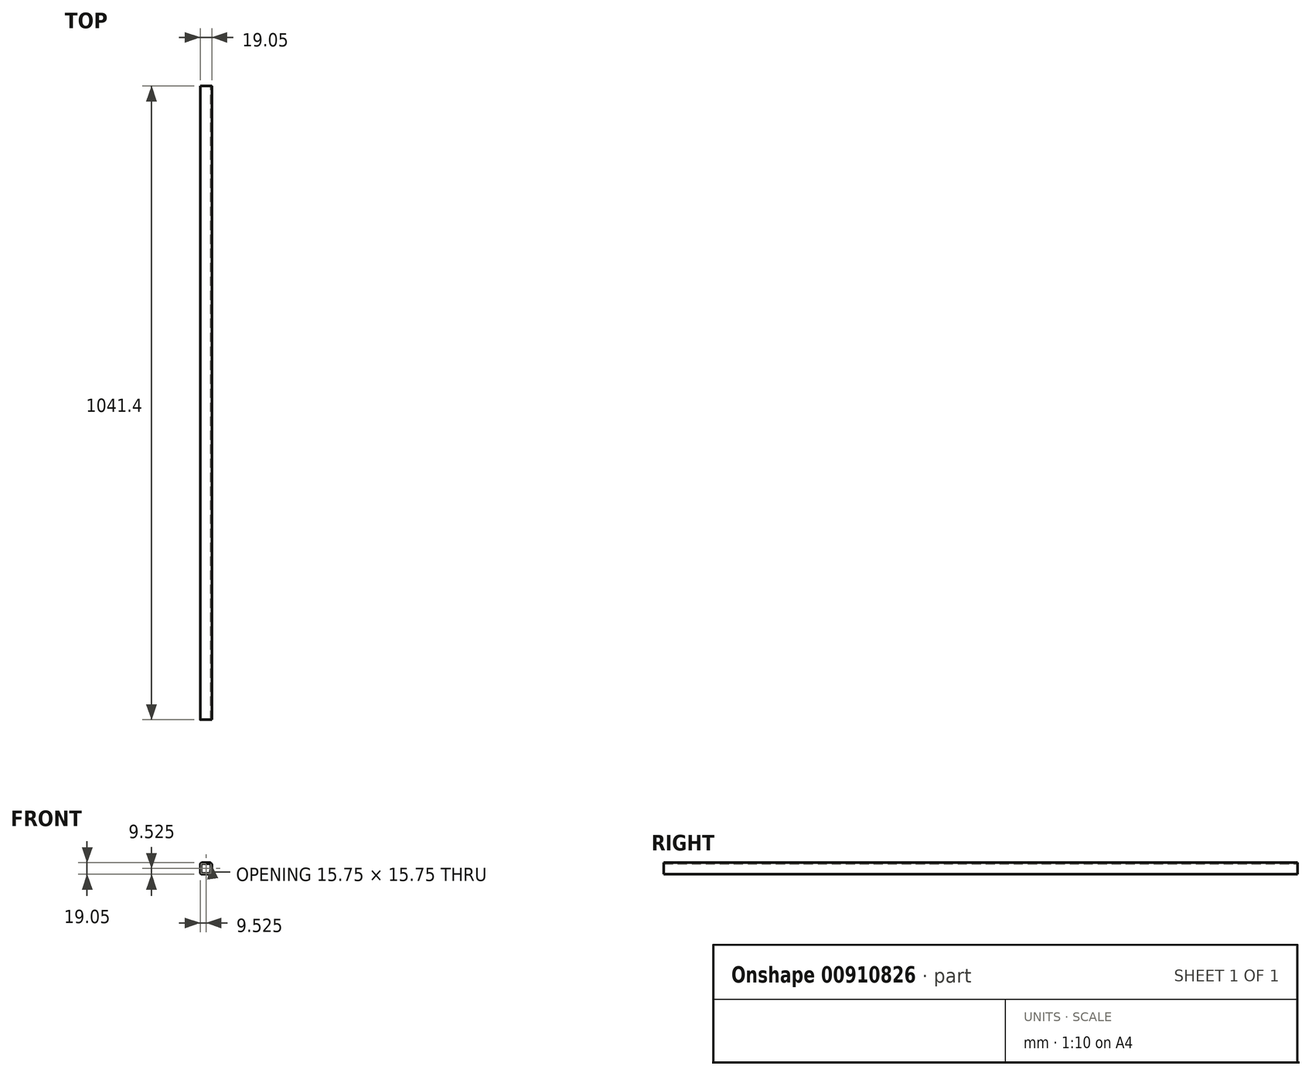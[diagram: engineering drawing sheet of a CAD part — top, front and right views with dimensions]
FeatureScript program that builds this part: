
annotation { "Feature Type Name" : "Feature", "Feature Type Description" : "" }
export const myFeature = defineFeature(function(context is Context, id is Id, definition is map)
    precondition{}
    {
        {
            var Q0;
            Q0=qCreatedBy(makeId("Front.planeOp"),FACE);
            var sketch = newSketch(context, id + "F0", { "sketchPlane" : qUnion([Q0])});
            skLineSegment(sketch, "E0.bottom", {"start": v(3.18, 0) * mm, "end": v(15.87, 0) * mm});
            skLineSegment(sketch, "E0.top", {"start": v(3.17, 19.05) * mm, "end": v(15.88, 19.05) * mm});
            skLineSegment(sketch, "E0.left", {"start": v(0, 3.17) * mm, "end": v(0, 15.88) * mm});
            skLineSegment(sketch, "E0.right", {"start": v(19.05, 3.18) * mm, "end": v(19.05, 15.88) * mm});
            skPoint(sketch, "E1.visualSharp", {"position": v(0, 19.05) * mm});
            skArc(sketch, "E1.filletArc", {"start": v(3.17, 19.05) * mm, "mid": v(0.93, 18.12) * mm, "end": v(0, 15.88) * mm});
            skPoint(sketch, "E2.visualSharp", {"position": v(19.05, 19.05) * mm});
            skArc(sketch, "E2.filletArc", {"start": v(19.05, 15.88) * mm, "mid": v(18.12, 18.12) * mm, "end": v(15.88, 19.05) * mm});
            skPoint(sketch, "E3.visualSharp", {"position": v(19.05, 0) * mm});
            skArc(sketch, "E3.filletArc", {"start": v(15.87, 0) * mm, "mid": v(18.12, 0.93) * mm, "end": v(19.05, 3.18) * mm});
            skPoint(sketch, "E4.visualSharp", {"position": v(0, 0) * mm});
            skArc(sketch, "E4.filletArc", {"start": v(0, 3.17) * mm, "mid": v(0.93, 0.93) * mm, "end": v(3.18, 0) * mm});
            skLineSegment(sketch, "E5.0", {"start": v(17.4, 3.3) * mm, "end": v(17.4, 15.75) * mm});
            skLineSegment(sketch, "E5.1", {"start": v(3.3, 1.65) * mm, "end": v(15.75, 1.65) * mm});
            skLineSegment(sketch, "E5.2", {"start": v(1.65, 3.3) * mm, "end": v(1.65, 15.75) * mm});
            skLineSegment(sketch, "E5.3", {"start": v(3.3, 17.4) * mm, "end": v(15.75, 17.4) * mm});
            skPoint(sketch, "E6.visualSharp", {"position": v(17.4, 17.4) * mm});
            skArc(sketch, "E6.filletArc", {"start": v(17.4, 15.75) * mm, "mid": v(16.92, 16.92) * mm, "end": v(15.75, 17.4) * mm});
            skPoint(sketch, "E7.visualSharp", {"position": v(1.65, 17.4) * mm});
            skArc(sketch, "E7.filletArc", {"start": v(3.3, 17.4) * mm, "mid": v(2.13, 16.92) * mm, "end": v(1.65, 15.75) * mm});
            skPoint(sketch, "E8.visualSharp", {"position": v(1.65, 1.65) * mm});
            skArc(sketch, "E8.filletArc", {"start": v(1.65, 3.3) * mm, "mid": v(2.13, 2.13) * mm, "end": v(3.3, 1.65) * mm});
            skPoint(sketch, "E9.visualSharp", {"position": v(17.4, 1.65) * mm});
            skArc(sketch, "E9.filletArc", {"start": v(15.75, 1.65) * mm, "mid": v(16.92, 2.13) * mm, "end": v(17.4, 3.3) * mm});
            skSolve(sketch);
        }
        {
            var Q0;
            Q0 = qSketchRegion(id + "F0", true);
            extrude(context, id + "F1", {"entities" : qUnion([Q0]), "depth" : 1041.4 * mm, "offsetDistance" : 25.4 * mm});
        }
    });
